# Revit family: Mélange Gaz 1000L VERTICAL
name_source: partatom
category: Modèles génériques
units: mm (PartAtom-declared; Revit-internal decimal feet)

## family parameters
Basée sur le plan de construction = Non
Cote de connecteur circulaire = Utiliser le diamètre
Couper avec des vides une fois chargée = Non
Partagée = Non
Peut héberger une armature = Non
Repere pour localisation dans la piece = Non
Toujours verticalement = Oui
Type d'élément = Normal

## types (2) — shared parameters
Rayon Cuve = 425 mm  [stored 1.39436 ft]
Ø Diamètre Cuve = 850 mm  [stored 2.78871 ft]
zero-valued in all types: Elévation par défaut

## per-type parameters (varying)
| type | Hauteur de pied | Ht Fond bombé | Ht ballon sans pied |
| 500L | 421 mm  [stored 1.38123 ft] | 277 mm  [stored 0.908793 ft] | 2054 mm  [stored 6.73885 ft] |
| 200L | 317 mm  [stored 1.04003 ft] | 173 mm  [stored 0.567585 ft] | 1310 mm  [stored 4.2979 ft] |

note: [stored X ft] marks values corroborated as IEEE doubles in the binary element streams (Revit-internal decimal feet)
